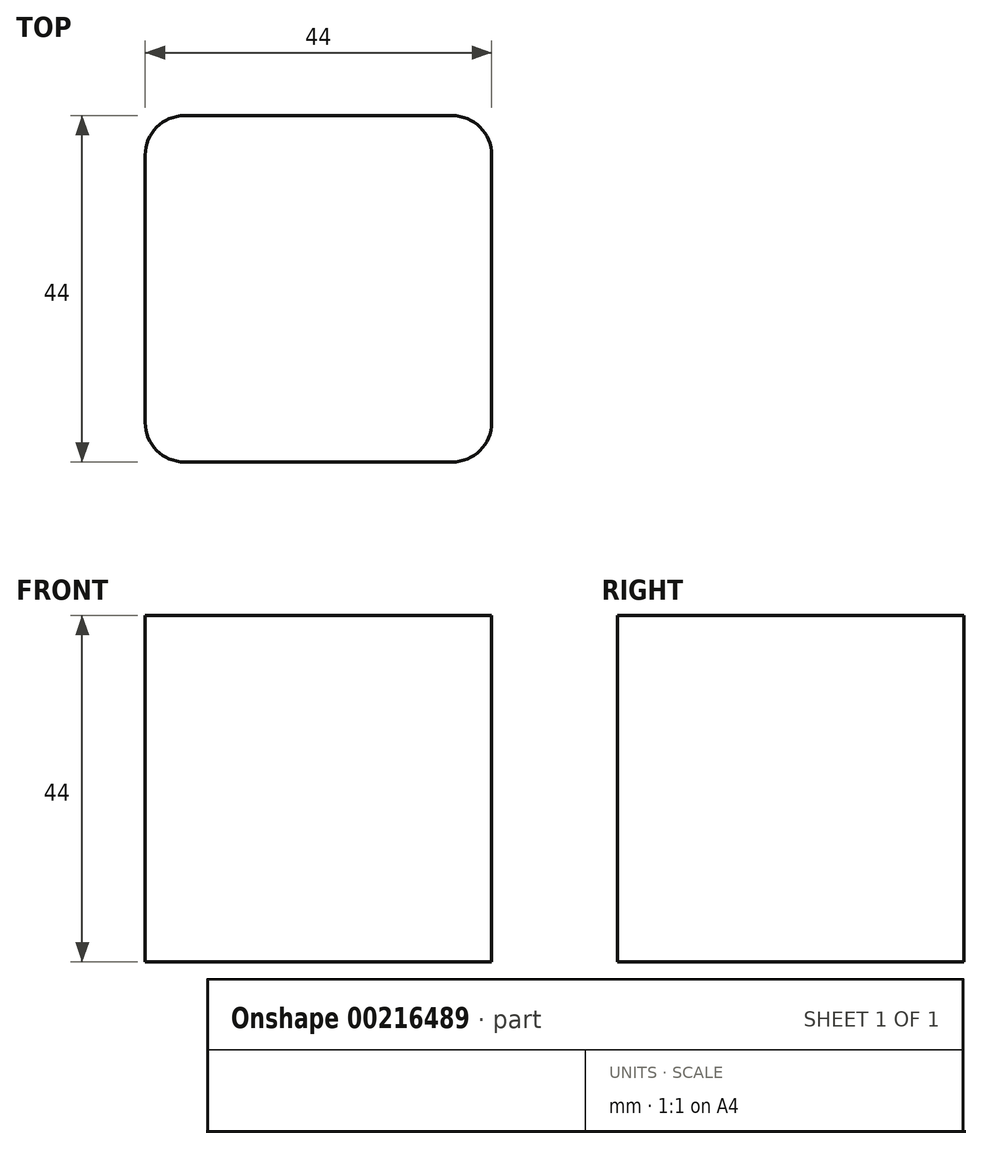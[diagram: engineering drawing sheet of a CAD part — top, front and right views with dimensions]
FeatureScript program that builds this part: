
annotation { "Feature Type Name" : "Feature", "Feature Type Description" : "" }
export const myFeature = defineFeature(function(context is Context, id is Id, definition is map)
    precondition{}
    {
        {
            assignVariable(context, id + "F0", {"name" : "Side", "anyValue" : 44});
        }
        {
            var Q0;
            Q0=qCreatedBy(makeId("Top.planeOp"),FACE);
            var sketch = newSketch(context, id + "F1", { "sketchPlane" : qUnion([Q0])});
            skLineSegment(sketch, "E0.bottom", {"start": v(22, 22) * mm, "end": v(-22, 22) * mm});
            skLineSegment(sketch, "E0.top", {"start": v(22, -22) * mm, "end": v(-22, -22) * mm});
            skLineSegment(sketch, "E0.left", {"start": v(22, 22) * mm, "end": v(22, -22) * mm});
            skLineSegment(sketch, "E0.right", {"start": v(-22, 22) * mm, "end": v(-22, -22) * mm});
            skPoint(sketch, "E0.middle", {"position": v(0, 0) * mm});
            skSolve(sketch);
        }
        {
            var Q0;
            Q0=qSketchRegion(id+"F1",true);
            extrude(context, id + "F2", {"entities" : qUnion([Q0]), "depth" : (getVariable(context, 'Side')) * mm, "offsetDistance" : 25 * mm});
        }
        {
            var Q0;
            Q0=makeQuery(id+"F2.opExtrude","SWEPT_EDGE",EDGE,{"disambiguationData":[OSD([sQuery(id+"F1.wireOp",EDGE,"E0.top"),sQuery(id+"F1.wireOp",EDGE,"E0.left")])]});
            var Q1;
            Q1=makeQuery(id+"F2.opExtrude","SWEPT_EDGE",EDGE,{"disambiguationData":[OSD([sQuery(id+"F1.wireOp",EDGE,"E0.bottom"),sQuery(id+"F1.wireOp",EDGE,"E0.left")])]});
            var Q2;
            Q2=makeQuery(id+"F2.opExtrude","SWEPT_EDGE",EDGE,{"disambiguationData":[OSD([sQuery(id+"F1.wireOp",EDGE,"E0.top"),sQuery(id+"F1.wireOp",EDGE,"E0.right")])]});
            var Q3;
            Q3=makeQuery(id+"F2.opExtrude","SWEPT_EDGE",EDGE,{"disambiguationData":[OSD([sQuery(id+"F1.wireOp",EDGE,"E0.bottom"),sQuery(id+"F1.wireOp",EDGE,"E0.right")])]});
            fillet(context, id + "F3", {"entities" : qUnion([Q0, Q1, Q2, Q3]), "radius" : 5 * mm, "tangentPropagation" : true, "allowEdgeOverflow" : false});
        }
    });
